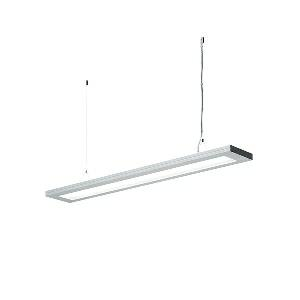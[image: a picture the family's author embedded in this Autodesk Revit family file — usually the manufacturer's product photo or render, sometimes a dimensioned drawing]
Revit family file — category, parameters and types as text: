
# Revit family: lavigo_-_dpp_16000_840_d_g2_00750545_7ebc
name_source: partatom
category: Lighting Fixtures
units: mm (PartAtom-declared; Revit-internal decimal feet)

## family parameters
Cut with Voids When Loaded = No
Host = Face
Light Source = No
Part Type = Normal
Room Calculation Point = No
Round Connector Dimension = Use Diameter
Shared = No

## types (1)
- LAVIGO - DPP 16000/840/D/G2 (1 x LED, 16450 lm, 4000K)
    Apparent Load = 112 VA
    Approval mark = CE
    CIE Flux Codes = 60 87 97 11 100
    Color Rendering = 80-89
    Color Temperature = 4000K
    Control Gear = Electronic ballast
    Default Elevation = 1800 mm
    Description = DPP 16000/840/D/G2|Suspended luminaire|light source: LED|connected load: 220-240V, 50/60Hz|Power consumption: approx. 112 W|standby: approx. 0,50|luminous flux: 16450 lm|luminous efficacy: 146 lm/W|light distribution: Direct/indirect|direct ratio: approx. 11 %|colour temperature: Cold white, ca. 4000 K|color rendering index (CRI): >= 80|chromaticity tolerance:  3 SDCM|System of protection: IP 20|technology: Continuously dimmable|luminaire body|material: Steel/plastic|surface: Powder coatet|colour: White|lamp cover: Polycarbonate (PC), Clear|mains lead: 1.00 m With free stranded wires|Fastening: Steel cable 0.3 - 0.7 m|decorative contrast side parts: Flint grey|glare control: Prism aperture|luminance(L65): <= 2800 cd/m|unified glare rating(4H 8H): <=  16|special features: Canopy colour (pure white), Cradle to Cradle Certified TM, DALI - dimming via digital rotary dimmer, DALI Load 3x, Direct light component with edge light and light-guide technology for homogenous light exit, Integration into DALI light management systems, Flicker-free, TouchDIM - dimming via standard switch|
    Frequency = 50 Hz
    Height = 36 mm
    Lamp = 1 x LED
    Lamp Light Flux = 16450 lm
    Lamp count = 1
    Length = 1245 mm
    Luminous efficacy = 147 lm/W
    Manufacturer = Waldmann
    ModVariant = No
    Model = 00750545
    Mounting Place = Ceiling
    Mounting Type = Pendant
    Number of Poles = 1
    OnlyDefault = Yes
    Power Factor = 1
    Product Name = LAVIGO - DPP 16000/840/D/G2
    Product group = Suspended luminaire
    ProductGroupID = 9
    Protection Class = Protection class I
    Protection Degree = IP 20
    RLX_Detail_Level = 1
    RLX_Emergency_Light_Flux = 0 lm
    RLX_Emergency_Type = 0
    RLX_Emergency_Type_DB = No
    RlxData = <blob elided: 24109 chars, md5=61fea644>
    Socket = socket
    Standby Power = 0 W
    System Light Flux = 16451 lm
    System Power = 112 W
    Type Comments = Product without accessories
    Type Image = 121740000-00678744.jpg
    URL = http://relux.com
    VarID = ---
    Voltage = 230 V
    Voltage Range = 220-240 V
    Weight = 0.00 kg
    Width = 200 mm  [stored 0.656168 ft]

note: [stored X ft] marks values corroborated as IEEE doubles in the binary element streams (Revit-internal decimal feet)

## geometry (parser evidence)
native form markers: Blend x4, Sweep x15
no freeform markers — native parametric forms only
